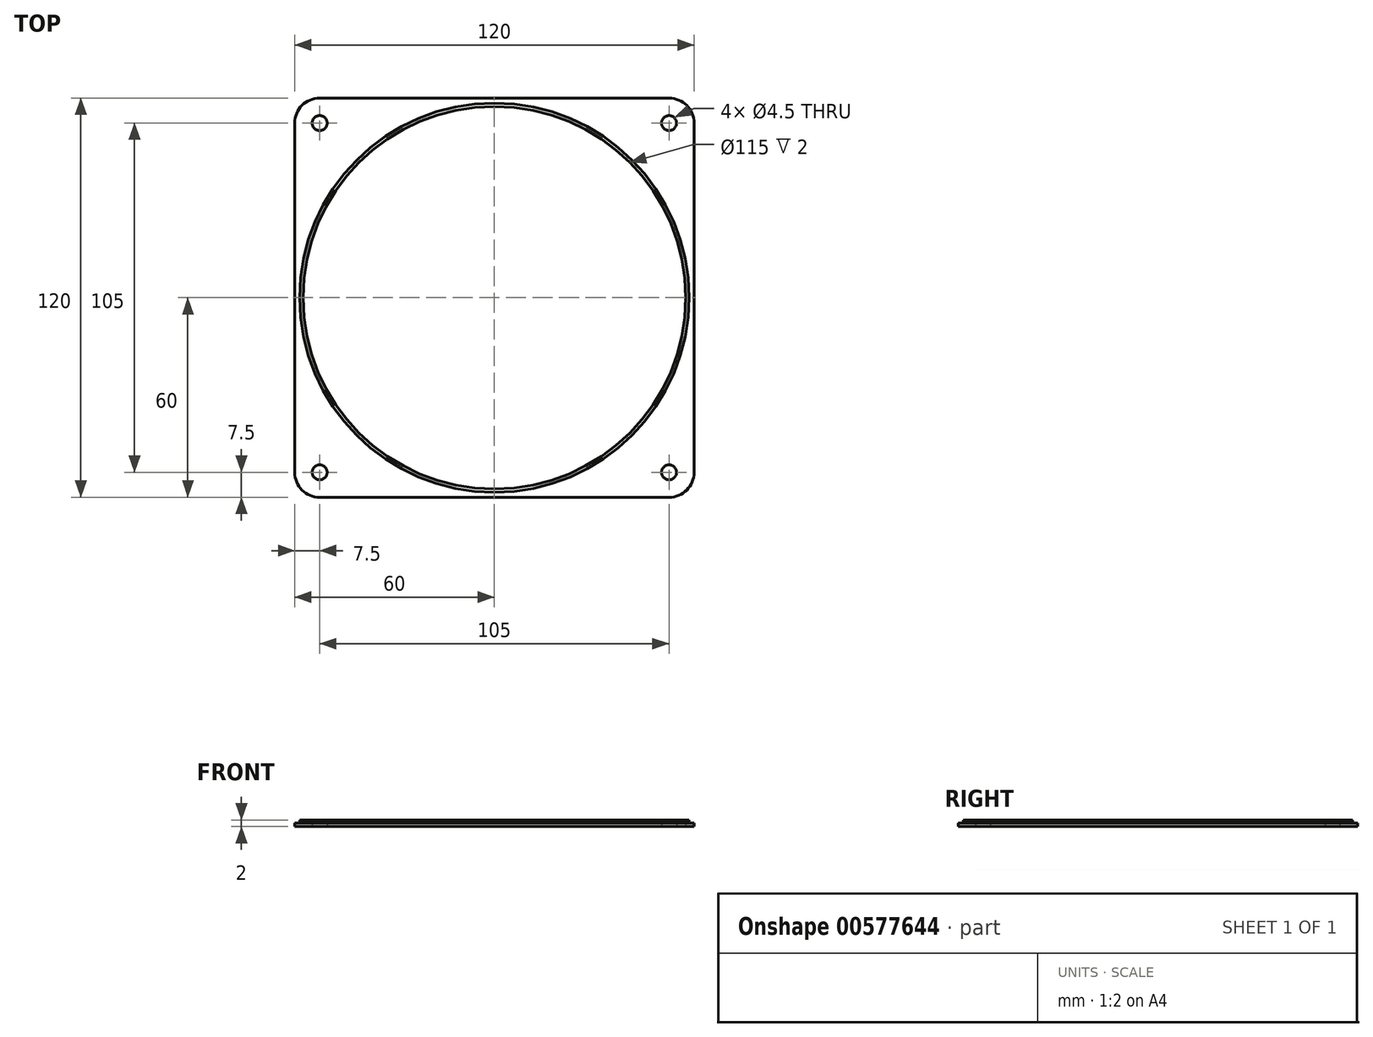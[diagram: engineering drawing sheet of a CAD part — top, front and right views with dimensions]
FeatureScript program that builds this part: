
annotation { "Feature Type Name" : "Feature", "Feature Type Description" : "" }
export const myFeature = defineFeature(function(context is Context, id is Id, definition is map)
    precondition{}
    {
        {
            var Q0;
            Q0=qCreatedBy(makeId("Top.planeOp"),FACE);
            var sketch = newSketch(context, id + "F0", { "sketchPlane" : qUnion([Q0])});
            skLineSegment(sketch, "E0.0", {"start": v(-52.5, 60) * mm, "end": v(52.5, 60) * mm});
            skLineSegment(sketch, "E0.1", {"start": v(-60, -52.5) * mm, "end": v(-60, 52.5) * mm});
            skLineSegment(sketch, "E0.2", {"start": v(-52.5, -60) * mm, "end": v(52.5, -60) * mm});
            skLineSegment(sketch, "E0.3", {"start": v(60, -52.5) * mm, "end": v(60, 52.5) * mm});
            skArc(sketch, "E1", {"start": v(52.5, 60) * mm, "mid": v(57.8, 57.8) * mm, "end": v(60, 52.5) * mm});
            skArc(sketch, "E2.1.1", {"start": v(-60, 52.5) * mm, "mid": v(-57.8, 57.8) * mm, "end": v(-52.5, 60) * mm});
            skArc(sketch, "E2.2.1", {"start": v(-52.5, -60) * mm, "mid": v(-57.8, -57.8) * mm, "end": v(-60, -52.5) * mm});
            skArc(sketch, "E2.3.1", {"start": v(60, -52.5) * mm, "mid": v(57.8, -57.8) * mm, "end": v(52.5, -60) * mm});
            skPoint(sketch, "E2.center", {"position": v(0, 0) * mm});
            skCircle(sketch, "E3", {"center": v(0, 0) * mm, "radius": 57.5 * mm});
            skCircle(sketch, "E4", {"center": v(-52.5, 52.5) * mm, "radius": 2.25 * mm});
            skCircle(sketch, "E5", {"center": v(52.5, 52.5) * mm, "radius": 2.25 * mm});
            skCircle(sketch, "E6", {"center": v(52.5, -52.5) * mm, "radius": 2.25 * mm});
            skCircle(sketch, "E7", {"center": v(-52.5, -52.5) * mm, "radius": 2.25 * mm});
            skCircle(sketch, "E8.0", {"center": v(0, 0) * mm, "radius": 58.5 * mm});
            skSolve(sketch);
        }
        {
            var Q0;
            Q0=qSketchRegion(id+"F0",true);
            extrude(context, id + "F1", {"entities" : qUnion([Q0]), "depth" : 1 * mm, "offsetDistance" : 25 * mm});
        }
        {
            var Q0;
            Q0=makeQuery(id+"F0.imprint","IMPRINT",FACE,{"disambiguationData":[TD([[makeQuery(id+"F0.imprint","IMPRINT",EDGE,{"derivedFrom":sQuery(id+"F0.wireOp",EDGE,"E3")}),-1.0]])]});
            extrude(context, id + "F2", {"entities" : qUnion([Q0]), "operationType" : NewBodyOperationType.ADD, "depth" : 2 * mm, "offsetDistance" : 25 * mm});
        }
    });
